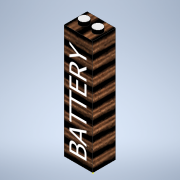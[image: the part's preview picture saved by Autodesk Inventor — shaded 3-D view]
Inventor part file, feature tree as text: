
AUTODESK INVENTOR PART (.ipt)
format: ipt  version: 2021 (Build 250183000, 183)  size: 128,000 bytes
history: native  units: mm
features: sketch x3, extrude x2
ambient origin geometry x8: Origin, YZ Plane, XZ Plane, XY Plane, X Axis, Y Axis, Z Axis, Center Point
bodies: Solid1 (feature_tree)
feature tree (5):
  extrude  "Extrusion1"  Depth=15.0mm
  extrude  "Extrusion2"  Depth=2.0mm TaperAngle=0.0deg
  sketch  "Sketch3"
  sketch  "Sketch1"  dims[d0=12.0mm d1=15.0mm]
  sketch  "Sketch2"  dims[d2=60.0mm d3=0.0mm d4=2.0mm d5=0.0mm]
